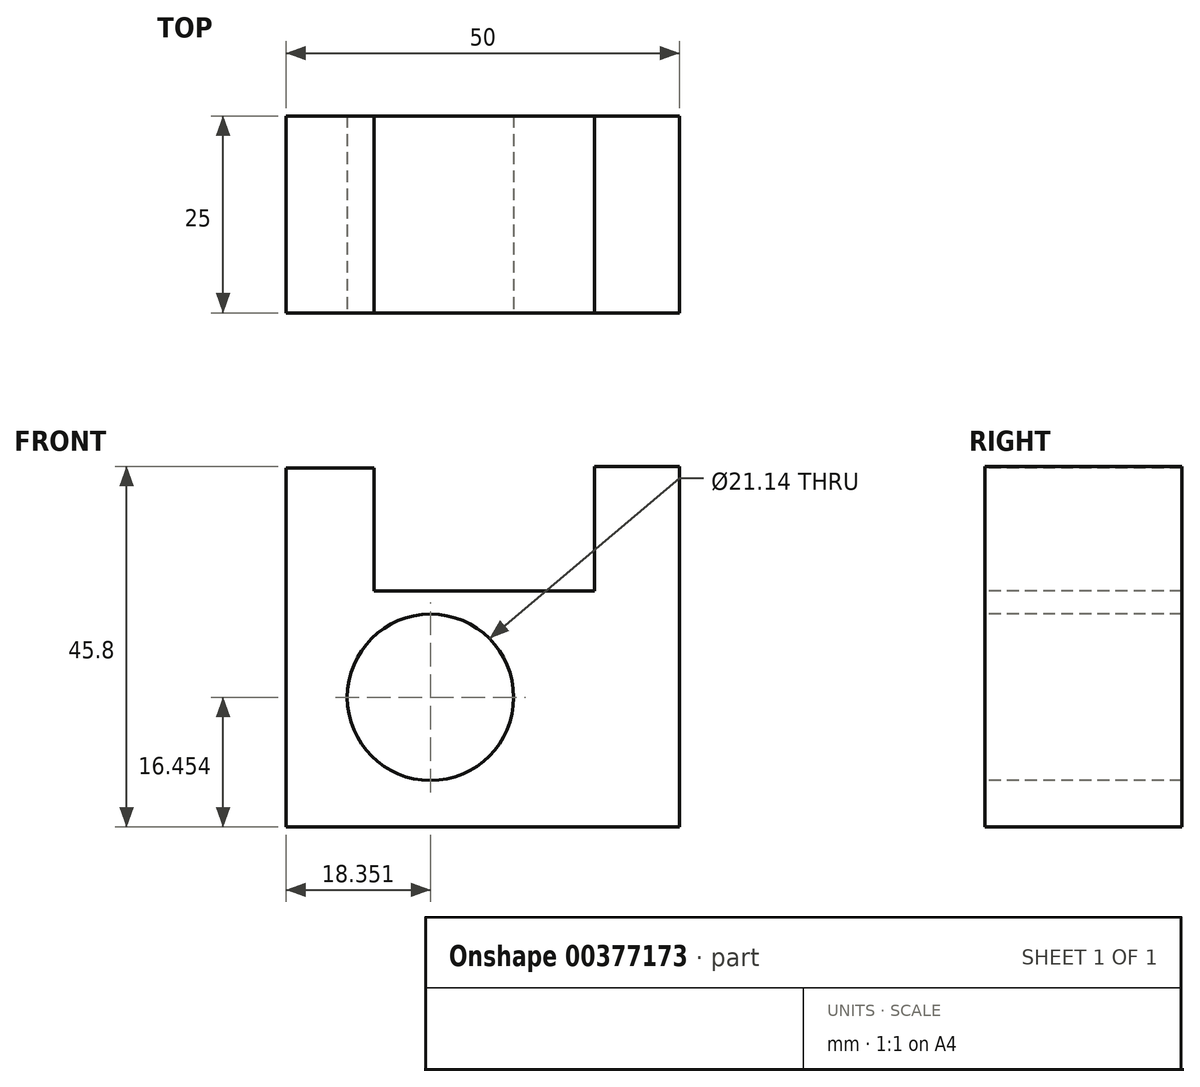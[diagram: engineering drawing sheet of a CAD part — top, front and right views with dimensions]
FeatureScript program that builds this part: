
annotation { "Feature Type Name" : "Feature", "Feature Type Description" : "" }
export const myFeature = defineFeature(function(context is Context, id is Id, definition is map)
    precondition{}
    {
        {
            var Q0;
            Q0=qCreatedBy(makeId("Front.planeOp"),FACE);
            var sketch = newSketch(context, id + "F0", { "sketchPlane" : qUnion([Q0])});
            skLineSegment(sketch, "E0.bottom", {"start": v(-23.28, 4.27) * mm, "end": v(26.72, 4.27) * mm});
            skLineSegment(sketch, "E0.top", {"start": v(-23.28, 34.27) * mm, "end": v(26.72, 34.27) * mm});
            skLineSegment(sketch, "E0.left", {"start": v(-23.28, 4.27) * mm, "end": v(-23.28, 34.27) * mm});
            skLineSegment(sketch, "E0.right", {"start": v(26.72, 4.27) * mm, "end": v(26.72, 34.27) * mm});
            skSolve(sketch);
        }
        {
            var Q0;
            Q0 = qSketchRegion(id + "F0", true);
            extrude(context, id + "F1", {"entities" : qUnion([Q0]), "depth" : 25 * mm});
        }
        {
            var Q0;
            Q0=makeQuery(id+"F1.opExtrude","CAP_FACE",FACE,{"disambiguationData":[OSD([sQuery(id+"F0.wireOp",EDGE,"E0.bottom"),sQuery(id+"F0.wireOp",EDGE,"E0.top"),sQuery(id+"F0.wireOp",EDGE,"E0.left"),sQuery(id+"F0.wireOp",EDGE,"E0.right")])],"isStart":false});
            var sketch = newSketch(context, id + "F2", { "sketchPlane" : qUnion([Q0])});
            skCircle(sketch, "E1", {"center": v(-4.93, 20.72) * mm, "radius": 10.57 * mm});
            skSolve(sketch);
        }
        {
            var Q0;
            Q0=makeQuery(id+"F2.imprint","IMPRINT",FACE,{"disambiguationData":[TD([[makeQuery(id+"F2.imprint","IMPRINT",EDGE,{"derivedFrom":sQuery(id+"F2.wireOp",EDGE,"E1")}),1.0]])]});
            extrude(context, id + "F3", {"entities" : qUnion([Q0]), "operationType" : NewBodyOperationType.REMOVE, "oppositeDirection" : true, "depth" : 25 * mm});
        }
        {
            var Q0;
            Q0=makeQuery(id+"F1.opExtrude","CAP_FACE",FACE,{"disambiguationData":[OSD([sQuery(id+"F0.wireOp",EDGE,"E0.bottom"),sQuery(id+"F0.wireOp",EDGE,"E0.top"),sQuery(id+"F0.wireOp",EDGE,"E0.left"),sQuery(id+"F0.wireOp",EDGE,"E0.right")])],"isStart":false});
            var sketch = newSketch(context, id + "F4", { "sketchPlane" : qUnion([Q0])});
            skLineSegment(sketch, "E2.bottom", {"start": v(-23.28, 34.27) * mm, "end": v(-12.1, 34.27) * mm});
            skLineSegment(sketch, "E2.top", {"start": v(-23.28, 49.85) * mm, "end": v(-12.1, 49.85) * mm});
            skLineSegment(sketch, "E2.left", {"start": v(-23.28, 34.27) * mm, "end": v(-23.28, 49.85) * mm});
            skLineSegment(sketch, "E2.right", {"start": v(-12.1, 34.27) * mm, "end": v(-12.1, 49.85) * mm});
            skLineSegment(sketch, "E3.bottom", {"start": v(26.72, 34.27) * mm, "end": v(15.9, 34.27) * mm});
            skLineSegment(sketch, "E3.top", {"start": v(26.72, 50.07) * mm, "end": v(15.9, 50.07) * mm});
            skLineSegment(sketch, "E3.left", {"start": v(26.72, 34.27) * mm, "end": v(26.72, 50.07) * mm});
            skLineSegment(sketch, "E3.right", {"start": v(15.9, 34.27) * mm, "end": v(15.9, 50.07) * mm});
            skSolve(sketch);
        }
        {
            var Q0;
            Q0 = qSketchRegion(id + "F4", true);
            extrude(context, id + "F5", {"entities" : qUnion([Q0]), "operationType" : NewBodyOperationType.ADD, "depth" : -25 * mm});
        }
    });
